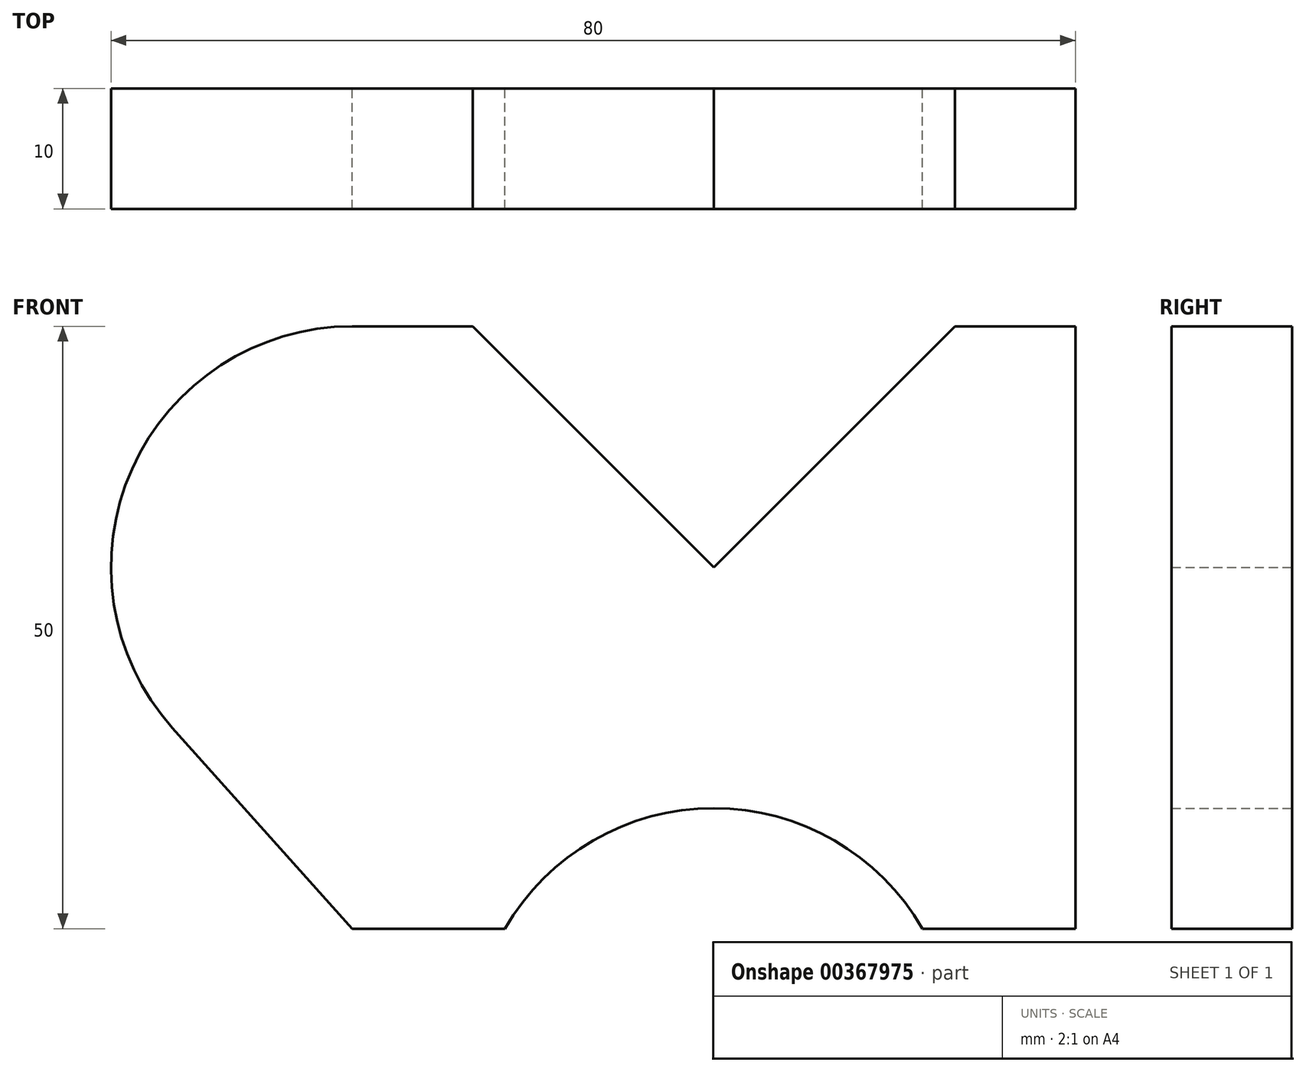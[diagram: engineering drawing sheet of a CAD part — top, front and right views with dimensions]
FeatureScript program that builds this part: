
annotation { "Feature Type Name" : "Feature", "Feature Type Description" : "" }
export const myFeature = defineFeature(function(context is Context, id is Id, definition is map)
    precondition{}
    {
        {
            var Q0;
            Q0=qCreatedBy(makeId("Front.planeOp"),FACE);
            var sketch = newSketch(context, id + "F0", { "sketchPlane" : qUnion([Q0])});
            skLineSegment(sketch, "E0", {"start": v(0, 0) * mm, "end": v(20, 20) * mm});
            skLineSegment(sketch, "E1", {"start": v(20, 20) * mm, "end": v(30, 20) * mm});
            skLineSegment(sketch, "E2", {"start": v(30, 20) * mm, "end": v(30, 0) * mm});
            skLineSegment(sketch, "E3", {"start": v(30, 0) * mm, "end": v(30, -30) * mm});
            skLineSegment(sketch, "E4", {"start": v(30, -30) * mm, "end": v(17.32, -30) * mm});
            skArc(sketch, "E5", {"start": v(17.32, -30) * mm, "mid": v(0, -20) * mm, "end": v(-17.32, -30) * mm});
            skLineSegment(sketch, "E6", {"start": v(-17.32, -30) * mm, "end": v(-30, -30) * mm});
            skLineSegment(sketch, "E7", {"start": v(-30, -30) * mm, "end": v(-44.9, -13.33) * mm});
            skLineSegment(sketch, "E8", {"start": v(0, 0) * mm, "end": v(-20, 20) * mm});
            skLineSegment(sketch, "E9", {"start": v(-20, 20) * mm, "end": v(-30, 20) * mm});
            skLineSegment(sketch, "E10", {"start": v(-30, 20) * mm, "end": v(-30, 20) * mm});
            skArc(sketch, "E11", {"start": v(-30, 20) * mm, "mid": v(-48.26, 8.16) * mm, "end": v(-44.9, -13.33) * mm});
            skLineSegment(sketch, "E12", {"start": v(-30, 20) * mm, "end": v(-30, -30) * mm, "construction": true});
            skSolve(sketch);
        }
        {
            var Q0;
            Q0=makeQuery(id+"F0.imprint","IMPRINT",FACE,{"disambiguationData":[TD([[makeQuery(id+"F0.imprint","IMPRINT",EDGE,{"derivedFrom":sQuery(id+"F0.wireOp",EDGE,"E0")}),-1.0]])]});
            extrude(context, id + "F1", {"entities" : qUnion([Q0]), "endBound" : BoundingType.SYMMETRIC, "depth" : 10 * mm, "offsetDistance" : 25 * mm});
        }
    });
